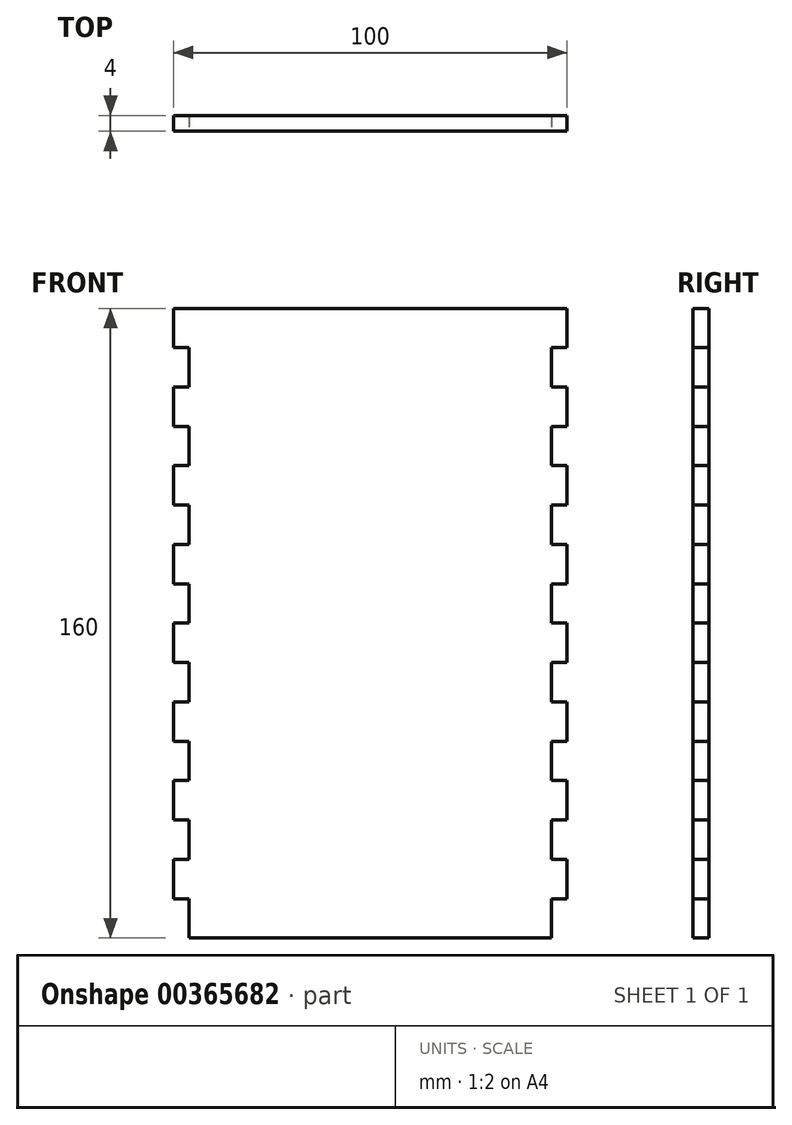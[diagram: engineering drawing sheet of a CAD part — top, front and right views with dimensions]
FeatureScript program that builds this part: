
annotation { "Feature Type Name" : "Feature", "Feature Type Description" : "" }
export const myFeature = defineFeature(function(context is Context, id is Id, definition is map)
    precondition{}
    {
        {
            var Q0;
            Q0=qCreatedBy(makeId("Front.planeOp"),FACE);
            var sketch = newSketch(context, id + "F0", { "sketchPlane" : qUnion([Q0])});
            skLineSegment(sketch, "E0.bottom", {"start": v(0, 0) * mm, "end": v(100, 0) * mm});
            skLineSegment(sketch, "E0.top", {"start": v(0, 160) * mm, "end": v(100, 160) * mm});
            skLineSegment(sketch, "E0.left", {"start": v(0, 0) * mm, "end": v(0, 160) * mm});
            skLineSegment(sketch, "E0.right", {"start": v(100, 0) * mm, "end": v(100, 160) * mm});
            skSolve(sketch);
        }
        {
            var Q0;
            Q0 = qSketchRegion(id + "F0", true);
            extrude(context, id + "F1", {"entities" : qUnion([Q0]), "depth" : 4 * mm});
        }
        {
            var Q0;
            Q0=makeQuery(id+"F1.opExtrude","CAP_FACE",FACE,{"disambiguationData":[OSD([sQuery(id+"F0.wireOp",EDGE,"E0.bottom"),sQuery(id+"F0.wireOp",EDGE,"E0.top"),sQuery(id+"F0.wireOp",EDGE,"E0.left"),sQuery(id+"F0.wireOp",EDGE,"E0.right")])],"isStart":false});
            var sketch = newSketch(context, id + "F2", { "sketchPlane" : qUnion([Q0])});
            skLineSegment(sketch, "E1.bottom", {"start": v(0, 0) * mm, "end": v(4, 0) * mm});
            skLineSegment(sketch, "E1.top", {"start": v(0, 10) * mm, "end": v(4, 10) * mm});
            skLineSegment(sketch, "E1.left", {"start": v(0, 0) * mm, "end": v(0, 10) * mm});
            skLineSegment(sketch, "E1.right", {"start": v(4, 0) * mm, "end": v(4, 10) * mm});
            skLineSegment(sketch, "E2.0.1.0", {"start": v(4, 20) * mm, "end": v(4, 30) * mm});
            skLineSegment(sketch, "E2.0.1.1", {"start": v(0, 20) * mm, "end": v(0, 30) * mm});
            skLineSegment(sketch, "E2.0.1.2", {"start": v(0, 30) * mm, "end": v(4, 30) * mm});
            skLineSegment(sketch, "E2.0.1.3", {"start": v(0, 20) * mm, "end": v(4, 20) * mm});
            skLineSegment(sketch, "E2.0.2.0", {"start": v(4, 40) * mm, "end": v(4, 50) * mm});
            skLineSegment(sketch, "E2.0.2.1", {"start": v(0, 40) * mm, "end": v(0, 50) * mm});
            skLineSegment(sketch, "E2.0.2.2", {"start": v(0, 50) * mm, "end": v(4, 50) * mm});
            skLineSegment(sketch, "E2.0.2.3", {"start": v(0, 40) * mm, "end": v(4, 40) * mm});
            skLineSegment(sketch, "E2.0.3.0", {"start": v(4, 60) * mm, "end": v(4, 70) * mm});
            skLineSegment(sketch, "E2.0.3.1", {"start": v(0, 60) * mm, "end": v(0, 70) * mm});
            skLineSegment(sketch, "E2.0.3.2", {"start": v(0, 70) * mm, "end": v(4, 70) * mm});
            skLineSegment(sketch, "E2.0.3.3", {"start": v(0, 60) * mm, "end": v(4, 60) * mm});
            skLineSegment(sketch, "E2.0.4.0", {"start": v(4, 80) * mm, "end": v(4, 90) * mm});
            skLineSegment(sketch, "E2.0.4.1", {"start": v(0, 80) * mm, "end": v(0, 90) * mm});
            skLineSegment(sketch, "E2.0.4.2", {"start": v(0, 90) * mm, "end": v(4, 90) * mm});
            skLineSegment(sketch, "E2.0.4.3", {"start": v(0, 80) * mm, "end": v(4, 80) * mm});
            skLineSegment(sketch, "E2.0.5.0", {"start": v(4, 100) * mm, "end": v(4, 110) * mm});
            skLineSegment(sketch, "E2.0.5.1", {"start": v(0, 100) * mm, "end": v(0, 110) * mm});
            skLineSegment(sketch, "E2.0.5.2", {"start": v(0, 110) * mm, "end": v(4, 110) * mm});
            skLineSegment(sketch, "E2.0.5.3", {"start": v(0, 100) * mm, "end": v(4, 100) * mm});
            skLineSegment(sketch, "E2.0.6.0", {"start": v(4, 120) * mm, "end": v(4, 130) * mm});
            skLineSegment(sketch, "E2.0.6.1", {"start": v(0, 120) * mm, "end": v(0, 130) * mm});
            skLineSegment(sketch, "E2.0.6.2", {"start": v(0, 130) * mm, "end": v(4, 130) * mm});
            skLineSegment(sketch, "E2.0.6.3", {"start": v(0, 120) * mm, "end": v(4, 120) * mm});
            skLineSegment(sketch, "E2.0.7.0", {"start": v(4, 140) * mm, "end": v(4, 150) * mm});
            skLineSegment(sketch, "E2.0.7.1", {"start": v(0, 140) * mm, "end": v(0, 150) * mm});
            skLineSegment(sketch, "E2.0.7.2", {"start": v(0, 150) * mm, "end": v(4, 150) * mm});
            skLineSegment(sketch, "E2.0.7.3", {"start": v(0, 140) * mm, "end": v(4, 140) * mm});
            skLineSegment(sketch, "E2.direction1", {"start": v(0, 0) * mm, "end": v(4, 0) * mm, "construction": true});
            skLineSegment(sketch, "E2.direction2", {"start": v(0, 0) * mm, "end": v(0, 20) * mm, "construction": true});
            skLineSegment(sketch, "E3", {"start": v(50, 0) * mm, "end": v(50, 160) * mm, "construction": true});
            skLineSegment(sketch, "E4.MirrorCS", {"start": v(100, 0) * mm, "end": v(96, 0) * mm});
            skLineSegment(sketch, "E5.MirrorCS", {"start": v(100, 0) * mm, "end": v(100, 20) * mm, "construction": true});
            skLineSegment(sketch, "E6.MirrorCS", {"start": v(100, 0) * mm, "end": v(96, 0) * mm, "construction": true});
            skLineSegment(sketch, "E7.MirrorCS", {"start": v(100, 120) * mm, "end": v(96, 120) * mm});
            skLineSegment(sketch, "E8.MirrorCS", {"start": v(100, 100) * mm, "end": v(96, 100) * mm});
            skLineSegment(sketch, "E9.MirrorCS", {"start": v(100, 150) * mm, "end": v(96, 150) * mm});
            skLineSegment(sketch, "E10.MirrorCS", {"start": v(100, 30) * mm, "end": v(96, 30) * mm});
            skLineSegment(sketch, "E11.MirrorCS", {"start": v(100, 10) * mm, "end": v(96, 10) * mm});
            skLineSegment(sketch, "E12.MirrorCS", {"start": v(100, 20) * mm, "end": v(96, 20) * mm});
            skLineSegment(sketch, "E13.MirrorCS", {"start": v(100, 60) * mm, "end": v(96, 60) * mm});
            skLineSegment(sketch, "E14.MirrorCS", {"start": v(100, 130) * mm, "end": v(96, 130) * mm});
            skLineSegment(sketch, "E15.MirrorCS", {"start": v(100, 80) * mm, "end": v(96, 80) * mm});
            skLineSegment(sketch, "E16.MirrorCS", {"start": v(100, 50) * mm, "end": v(96, 50) * mm});
            skLineSegment(sketch, "E17.MirrorCS", {"start": v(100, 40) * mm, "end": v(96, 40) * mm});
            skLineSegment(sketch, "E18.MirrorCS", {"start": v(100, 70) * mm, "end": v(96, 70) * mm});
            skLineSegment(sketch, "E19.MirrorCS", {"start": v(100, 90) * mm, "end": v(96, 90) * mm});
            skLineSegment(sketch, "E20.MirrorCS", {"start": v(100, 110) * mm, "end": v(96, 110) * mm});
            skLineSegment(sketch, "E21.MirrorCS", {"start": v(100, 140) * mm, "end": v(96, 140) * mm});
            skLineSegment(sketch, "E22.MirrorCS", {"start": v(100, 0) * mm, "end": v(100, 10) * mm});
            skLineSegment(sketch, "E23.MirrorCS", {"start": v(100, 140) * mm, "end": v(100, 150) * mm});
            skLineSegment(sketch, "E24.MirrorCS", {"start": v(96, 100) * mm, "end": v(96, 110) * mm});
            skLineSegment(sketch, "E25.MirrorCS", {"start": v(96, 80) * mm, "end": v(96, 90) * mm});
            skLineSegment(sketch, "E26.MirrorCS", {"start": v(96, 140) * mm, "end": v(96, 150) * mm});
            skLineSegment(sketch, "E27.MirrorCS", {"start": v(96, 120) * mm, "end": v(96, 130) * mm});
            skLineSegment(sketch, "E28.MirrorCS", {"start": v(100, 100) * mm, "end": v(100, 110) * mm});
            skLineSegment(sketch, "E29.MirrorCS", {"start": v(100, 20) * mm, "end": v(100, 30) * mm});
            skLineSegment(sketch, "E30.MirrorCS", {"start": v(100, 80) * mm, "end": v(100, 90) * mm});
            skLineSegment(sketch, "E31.MirrorCS", {"start": v(96, 20) * mm, "end": v(96, 30) * mm});
            skLineSegment(sketch, "E32.MirrorCS", {"start": v(100, 60) * mm, "end": v(100, 70) * mm});
            skLineSegment(sketch, "E33.MirrorCS", {"start": v(96, 0) * mm, "end": v(96, 10) * mm});
            skLineSegment(sketch, "E34.MirrorCS", {"start": v(100, 40) * mm, "end": v(100, 50) * mm});
            skLineSegment(sketch, "E35.MirrorCS", {"start": v(96, 40) * mm, "end": v(96, 50) * mm});
            skLineSegment(sketch, "E36.MirrorCS", {"start": v(96, 60) * mm, "end": v(96, 70) * mm});
            skLineSegment(sketch, "E37.MirrorCS", {"start": v(100, 120) * mm, "end": v(100, 130) * mm});
            skSolve(sketch);
        }
        {
            var Q0;
            Q0 = qSketchRegion(id + "F2", true);
            extrude(context, id + "F3", {"entities" : qUnion([Q0]), "operationType" : NewBodyOperationType.REMOVE, "endBound" : BoundingType.UP_TO_NEXT, "oppositeDirection" : true, "depth" : 25 * mm});
        }
    });
